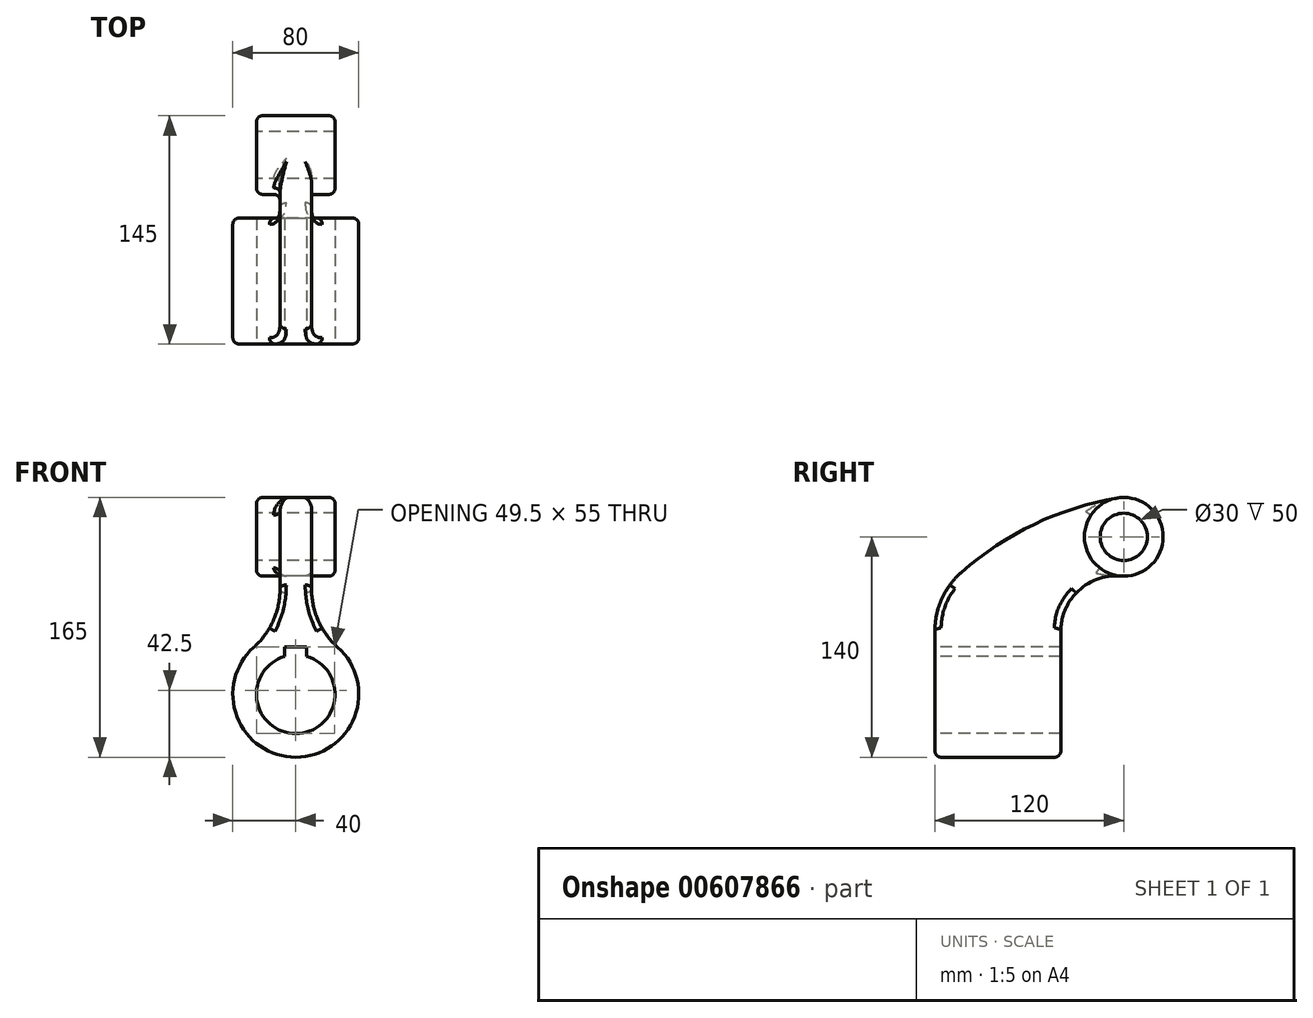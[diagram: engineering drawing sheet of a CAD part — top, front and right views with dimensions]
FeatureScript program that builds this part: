
annotation { "Feature Type Name" : "Feature", "Feature Type Description" : "" }
export const myFeature = defineFeature(function(context is Context, id is Id, definition is map)
    precondition{}
    {
        {
            var Q0;
            Q0=qCreatedBy(makeId("Right.planeOp"),FACE);
            var sketch = newSketch(context, id + "F0", { "sketchPlane" : qUnion([Q0])});
            skLineSegment(sketch, "E0", {"start": v(-80, 40) * mm, "end": v(-80, 25) * mm});
            skLineSegment(sketch, "E1", {"start": v(-80, 25) * mm, "end": v(0, 25) * mm});
            skLineSegment(sketch, "E2", {"start": v(0, 25) * mm, "end": v(0, 40) * mm});
            skLineSegment(sketch, "E3", {"start": v(0, 40) * mm, "end": v(-80, 40) * mm});
            skLineSegment(sketch, "E4", {"start": v(-153.76, 0) * mm, "end": v(0, 0) * mm, "construction": true});
            skCircle(sketch, "E5", {"center": v(40, 100) * mm, "radius": 25 * mm});
            skCircle(sketch, "E6", {"center": v(40, 100) * mm, "radius": 15 * mm});
            skArc(sketch, "E7", {"start": v(38, 75.08) * mm, "mid": v(11.32, 65.86) * mm, "end": v(0, 40) * mm});
            skArc(sketch, "E8", {"start": v(-63.05, 77.52) * mm, "mid": v(-75.57, 60.58) * mm, "end": v(-80, 40) * mm});
            skArc(sketch, "E9", {"start": v(35.84, 124.65) * mm, "mid": v(-16.9, 107.99) * mm, "end": v(-63.05, 77.52) * mm});
            skSolve(sketch);
        }
        {
            var Q0;
            Q0=makeQuery(id+"F0.imprint","IMPRINT",FACE,{"disambiguationData":[TD([[makeQuery(id+"F0.imprint","IMPRINT",EDGE,{"derivedFrom":sQuery(id+"F0.wireOp",EDGE,"E0")}),1.0]])]});
            var Q1;
            Q1=sQuery(id+"F0.wireOp",EDGE,"E4");
            revolve(context, id + "F1", {"entities" : qUnion([Q0]), "axis" : qUnion([Q1]), "revolveType" : RevolveType.FULL});
        }
        {
            var Q0;
            Q0=makeQuery(id+"F0.imprint","IMPRINT",FACE,{"disambiguationData":[TD([[makeQuery(id+"F0.imprint","IMPRINT",EDGE,{"derivedFrom":sQuery(id+"F0.wireOp",EDGE,"E3")}),-1.0]])]});
            var Q1;
            Q1=makeQuery(id+"F0.imprint","IMPRINT",FACE,{"disambiguationData":[TD([[makeQuery(id+"F0.imprint","IMPRINT",EDGE,{"derivedFrom":sQuery(id+"F0.wireOp",EDGE,"E0")}),1.0]])]});
            extrude(context, id + "F2", {"entities" : qUnion([Q0, Q1]), "operationType" : NewBodyOperationType.ADD, "endBound" : BoundingType.SYMMETRIC, "depth" : 20 * mm, "offsetDistance" : 25 * mm});
        }
        {
            var Q0;
            Q0=makeQuery(id+"F0.imprint","IMPRINT",FACE,{"disambiguationData":[TD([[makeQuery(id+"F0.imprint","IMPRINT",EDGE,{"derivedFrom":sQuery(id+"F0.wireOp",EDGE,"E6")}),-1.0]])]});
            extrude(context, id + "F3", {"entities" : qUnion([Q0]), "operationType" : NewBodyOperationType.ADD, "endBound" : BoundingType.SYMMETRIC, "depth" : 50 * mm, "offsetDistance" : 25 * mm});
        }
        {
            var Q0;
            Q0=makeQuery(id+"F2.boolean.opBoolean","INTERSECT",EDGE,{"derivedFrom":[makeQuery(id+"F1.opRevolve","SWEPT_FACE",FACE,{"disambiguationData":[OSD([sQuery(id+"F0.wireOp",EDGE,"E3")])]}),makeQuery(id+"F2.opExtrude","CAP_FACE",FACE,{"disambiguationData":[OSD([sQuery(id+"F0.wireOp",EDGE,"E0"),sQuery(id+"F0.wireOp",EDGE,"E1"),sQuery(id+"F0.wireOp",EDGE,"E2"),sQuery(id+"F0.wireOp",EDGE,"E5"),sQuery(id+"F0.wireOp",EDGE,"E7"),sQuery(id+"F0.wireOp",EDGE,"E8"),sQuery(id+"F0.wireOp",EDGE,"E9")])],"isStart":false})]});
            var Q1;
            Q1=makeQuery(id+"F2.boolean.opBoolean","INTERSECT",EDGE,{"derivedFrom":[makeQuery(id+"F1.opRevolve","SWEPT_FACE",FACE,{"disambiguationData":[OSD([sQuery(id+"F0.wireOp",EDGE,"E3")])]}),makeQuery(id+"F2.opExtrude","CAP_FACE",FACE,{"disambiguationData":[OSD([sQuery(id+"F0.wireOp",EDGE,"E0"),sQuery(id+"F0.wireOp",EDGE,"E1"),sQuery(id+"F0.wireOp",EDGE,"E2"),sQuery(id+"F0.wireOp",EDGE,"E5"),sQuery(id+"F0.wireOp",EDGE,"E7"),sQuery(id+"F0.wireOp",EDGE,"E8"),sQuery(id+"F0.wireOp",EDGE,"E9")])],"isStart":true})]});
            fillet(context, id + "F4", {"entities" : qUnion([Q0, Q1]), "radius" : 50 * mm, "tangentPropagation" : true, "allowEdgeOverflow" : false});
        }
        {
            var Q0;
            Q0=makeQuery(id+"F1.opRevolve","SWEPT_EDGE",EDGE,{"disambiguationData":[OSD([sQuery(id+"F0.wireOp",EDGE,"E0"),sQuery(id+"F0.wireOp",EDGE,"E3"),sQuery(id+"F0.wireOp",EDGE,"E8")])]});
            var Q1;
            Q1=makeQuery(id+"F2.opExtrude","CAP_EDGE",EDGE,{"disambiguationData":[OSD([sQuery(id+"F0.wireOp",EDGE,"E5")])],"isStart":false});
            var Q2;
            Q2=makeQuery(id+"F3.opExtrude","CAP_EDGE",EDGE,{"disambiguationData":[OSD([sQuery(id+"F0.wireOp",EDGE,"E5")])],"isStart":false});
            var Q3;
            Q3=makeQuery(id+"F2.opExtrude","CAP_FACE",FACE,{"disambiguationData":[OSD([sQuery(id+"F0.wireOp",EDGE,"E0"),sQuery(id+"F0.wireOp",EDGE,"E1"),sQuery(id+"F0.wireOp",EDGE,"E2"),sQuery(id+"F0.wireOp",EDGE,"E5"),sQuery(id+"F0.wireOp",EDGE,"E7"),sQuery(id+"F0.wireOp",EDGE,"E8"),sQuery(id+"F0.wireOp",EDGE,"E9")])],"isStart":true});
            var Q4;
            Q4=makeQuery(id+"F3.opExtrude","CAP_EDGE",EDGE,{"disambiguationData":[OSD([sQuery(id+"F0.wireOp",EDGE,"E5")])],"isStart":true});
            fillet(context, id + "F5", {"entities" : qUnion([Q0, Q1, Q2, Q3, Q4]), "radius" : 4 * mm, "tangentPropagation" : true, "allowEdgeOverflow" : false});
        }
        {
            var Q0;
            {var subQ0=sQuery(id+"F0.wireOp",EDGE,"E0");Q0=makeQuery(id+"F2.boolean.opBoolean","MERGE",FACE,{"derivedFrom":[makeQuery(id+"F1.opRevolve","SWEPT_FACE",FACE,{"disambiguationData":[OSD([subQ0])]}),makeQuery(id+"F2.opExtrude","SWEPT_FACE",FACE,{"disambiguationData":[OSD([subQ0])]})]});}
            var sketch = newSketch(context, id + "F6", { "sketchPlane" : qUnion([Q0])});
            skLineSegment(sketch, "E10", {"start": v(-7, 30) * mm, "end": v(7, 30) * mm});
            skLineSegment(sketch, "E11", {"start": v(7, 30) * mm, "end": v(7, 0) * mm});
            skLineSegment(sketch, "E12", {"start": v(7, 0) * mm, "end": v(-7, 0) * mm});
            skLineSegment(sketch, "E13", {"start": v(-7, 0) * mm, "end": v(-7, 30) * mm});
            skSolve(sketch);
        }
        {
            var Q0;
            {var subQ0=sQuery(id+"F6.wireOp",EDGE,"E10");Q0=makeQuery(id+"F6.imprint","IMPRINT",FACE,{"disambiguationData":[TD([[makeQuery(id+"F6.imprint","IMPRINT",EDGE,{"derivedFrom":subQ0}),-1.0]])]});}
            extrude(context, id + "F7", {"entities" : qUnion([Q0]), "operationType" : NewBodyOperationType.REMOVE, "oppositeDirection" : true, "depth" : 80 * mm, "offsetDistance" : 25 * mm});
        }
    });
